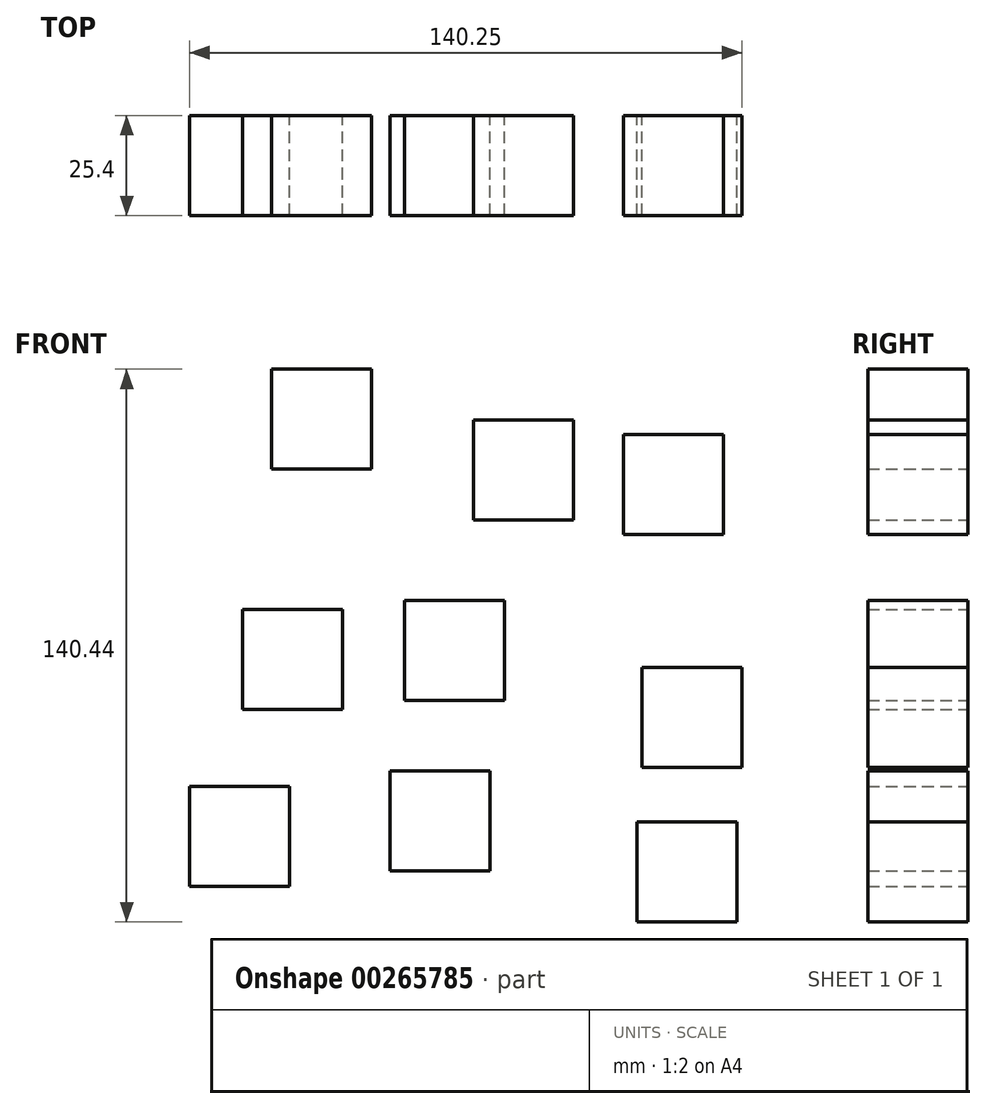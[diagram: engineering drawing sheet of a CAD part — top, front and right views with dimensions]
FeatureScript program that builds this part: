
annotation { "Feature Type Name" : "Feature", "Feature Type Description" : "" }
export const myFeature = defineFeature(function(context is Context, id is Id, definition is map)
    precondition{}
    {
        {
            var Q0;
            Q0=qCreatedBy(makeId("Front.planeOp"),FACE);
            var sketch = newSketch(context, id + "F0", { "sketchPlane" : qUnion([Q0])});
            skLineSegment(sketch, "E0.bottom", {"start": v(12.7, 12.7) * mm, "end": v(-12.7, 12.7) * mm});
            skLineSegment(sketch, "E0.top", {"start": v(12.7, -12.7) * mm, "end": v(-12.7, -12.7) * mm});
            skLineSegment(sketch, "E0.left", {"start": v(12.7, 12.7) * mm, "end": v(12.7, -12.7) * mm});
            skLineSegment(sketch, "E0.right", {"start": v(-12.7, 12.7) * mm, "end": v(-12.7, -12.7) * mm});
            skPoint(sketch, "E0.middle", {"position": v(0, 0) * mm});
            skLineSegment(sketch, "E1.bottom", {"start": v(-53.83, 10.47) * mm, "end": v(-28.43, 10.47) * mm});
            skLineSegment(sketch, "E1.top", {"start": v(-53.83, -14.93) * mm, "end": v(-28.43, -14.93) * mm});
            skLineSegment(sketch, "E1.left", {"start": v(-53.83, 10.47) * mm, "end": v(-53.83, -14.93) * mm});
            skLineSegment(sketch, "E1.right", {"start": v(-28.43, 10.47) * mm, "end": v(-28.43, -14.93) * mm});
            skLineSegment(sketch, "E2.bottom", {"start": v(-46.46, 71.49) * mm, "end": v(-21.06, 71.49) * mm});
            skLineSegment(sketch, "E2.top", {"start": v(-46.46, 46.09) * mm, "end": v(-21.06, 46.09) * mm});
            skLineSegment(sketch, "E2.left", {"start": v(-46.46, 71.49) * mm, "end": v(-46.46, 46.09) * mm});
            skLineSegment(sketch, "E2.right", {"start": v(-21.06, 71.49) * mm, "end": v(-21.06, 46.09) * mm});
            skLineSegment(sketch, "E3.bottom", {"start": v(42.95, 54.9) * mm, "end": v(68.35, 54.9) * mm});
            skLineSegment(sketch, "E3.top", {"start": v(42.95, 29.5) * mm, "end": v(68.35, 29.5) * mm});
            skLineSegment(sketch, "E3.left", {"start": v(42.95, 54.9) * mm, "end": v(42.95, 29.5) * mm});
            skLineSegment(sketch, "E3.right", {"start": v(68.35, 54.9) * mm, "end": v(68.35, 29.5) * mm});
            skLineSegment(sketch, "E4.bottom", {"start": v(47.56, -4.28) * mm, "end": v(72.96, -4.28) * mm});
            skLineSegment(sketch, "E4.top", {"start": v(47.56, -29.68) * mm, "end": v(72.96, -29.68) * mm});
            skLineSegment(sketch, "E4.left", {"start": v(47.56, -4.28) * mm, "end": v(47.56, -29.68) * mm});
            skLineSegment(sketch, "E4.right", {"start": v(72.96, -4.28) * mm, "end": v(72.96, -29.68) * mm});
            skLineSegment(sketch, "E5.bottom", {"start": v(-16.4, -30.64) * mm, "end": v(9, -30.64) * mm});
            skLineSegment(sketch, "E5.top", {"start": v(-16.4, -56.04) * mm, "end": v(9, -56.04) * mm});
            skLineSegment(sketch, "E5.left", {"start": v(-16.4, -30.64) * mm, "end": v(-16.4, -56.04) * mm});
            skLineSegment(sketch, "E5.right", {"start": v(9, -30.64) * mm, "end": v(9, -56.04) * mm});
            skLineSegment(sketch, "E6.bottom", {"start": v(4.8, 58.58) * mm, "end": v(30.2, 58.58) * mm});
            skLineSegment(sketch, "E6.top", {"start": v(4.8, 33.18) * mm, "end": v(30.2, 33.18) * mm});
            skLineSegment(sketch, "E6.left", {"start": v(4.8, 58.58) * mm, "end": v(4.8, 33.18) * mm});
            skLineSegment(sketch, "E6.right", {"start": v(30.2, 58.58) * mm, "end": v(30.2, 33.18) * mm});
            skLineSegment(sketch, "E7.bottom", {"start": v(-67.29, -34.52) * mm, "end": v(-41.89, -34.52) * mm});
            skLineSegment(sketch, "E7.top", {"start": v(-67.29, -59.92) * mm, "end": v(-41.89, -59.92) * mm});
            skLineSegment(sketch, "E7.left", {"start": v(-67.29, -34.52) * mm, "end": v(-67.29, -59.92) * mm});
            skLineSegment(sketch, "E7.right", {"start": v(-41.89, -34.52) * mm, "end": v(-41.89, -59.92) * mm});
            skLineSegment(sketch, "E8.bottom", {"start": v(46.27, -43.55) * mm, "end": v(71.67, -43.55) * mm});
            skLineSegment(sketch, "E8.top", {"start": v(46.27, -68.95) * mm, "end": v(71.67, -68.95) * mm});
            skLineSegment(sketch, "E8.left", {"start": v(46.27, -43.55) * mm, "end": v(46.27, -68.95) * mm});
            skLineSegment(sketch, "E8.right", {"start": v(71.67, -43.55) * mm, "end": v(71.67, -68.95) * mm});
            skSolve(sketch);
        }
        {
            var Q0;
            Q0=makeQuery(id+"F0.imprint","IMPRINT",FACE,{"disambiguationData":[TD([[makeQuery(id+"F0.imprint","IMPRINT",EDGE,{"derivedFrom":sQuery(id+"F0.wireOp",EDGE,"E2.bottom")}),-1.0]])]});
            var Q1;
            Q1=makeQuery(id+"F0.imprint","IMPRINT",FACE,{"disambiguationData":[TD([[makeQuery(id+"F0.imprint","IMPRINT",EDGE,{"derivedFrom":sQuery(id+"F0.wireOp",EDGE,"E6.bottom")}),-1.0]])]});
            var Q2;
            Q2=makeQuery(id+"F0.imprint","IMPRINT",FACE,{"disambiguationData":[TD([[makeQuery(id+"F0.imprint","IMPRINT",EDGE,{"derivedFrom":sQuery(id+"F0.wireOp",EDGE,"E3.bottom")}),-1.0]])]});
            var Q3;
            Q3=makeQuery(id+"F0.imprint","IMPRINT",FACE,{"disambiguationData":[TD([[makeQuery(id+"F0.imprint","IMPRINT",EDGE,{"derivedFrom":sQuery(id+"F0.wireOp",EDGE,"E4.bottom")}),-1.0]])]});
            var Q4;
            Q4=makeQuery(id+"F0.imprint","IMPRINT",FACE,{"disambiguationData":[TD([[makeQuery(id+"F0.imprint","IMPRINT",EDGE,{"derivedFrom":sQuery(id+"F0.wireOp",EDGE,"E8.bottom")}),-1.0]])]});
            var Q5;
            Q5=makeQuery(id+"F0.imprint","IMPRINT",FACE,{"disambiguationData":[TD([[makeQuery(id+"F0.imprint","IMPRINT",EDGE,{"derivedFrom":sQuery(id+"F0.wireOp",EDGE,"E5.bottom")}),-1.0]])]});
            var Q6;
            Q6=makeQuery(id+"F0.imprint","IMPRINT",FACE,{"disambiguationData":[TD([[makeQuery(id+"F0.imprint","IMPRINT",EDGE,{"derivedFrom":sQuery(id+"F0.wireOp",EDGE,"E0.bottom")}),1.0]])]});
            var Q7;
            Q7=makeQuery(id+"F0.imprint","IMPRINT",FACE,{"disambiguationData":[TD([[makeQuery(id+"F0.imprint","IMPRINT",EDGE,{"derivedFrom":sQuery(id+"F0.wireOp",EDGE,"E1.bottom")}),-1.0]])]});
            var Q8;
            Q8=makeQuery(id+"F0.imprint","IMPRINT",FACE,{"disambiguationData":[TD([[makeQuery(id+"F0.imprint","IMPRINT",EDGE,{"derivedFrom":sQuery(id+"F0.wireOp",EDGE,"E7.bottom")}),-1.0]])]});
            extrude(context, id + "F1", {"entities" : qUnion([Q0, Q1, Q2, Q3, Q4, Q5, Q6, Q7, Q8]), "depth" : 25.4 * mm});
        }
    });
